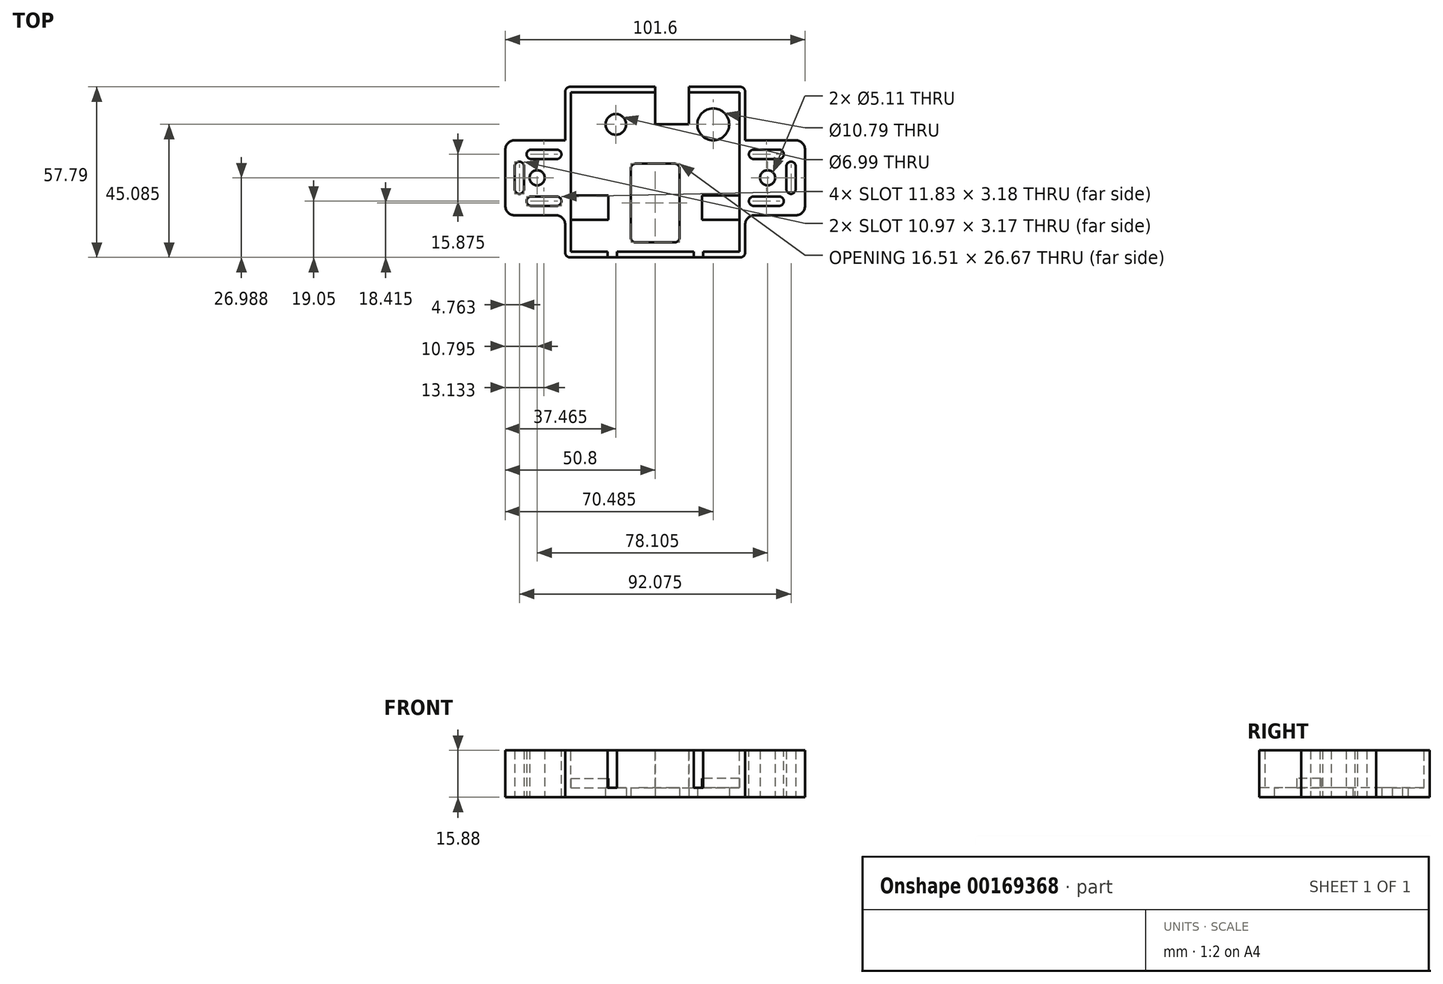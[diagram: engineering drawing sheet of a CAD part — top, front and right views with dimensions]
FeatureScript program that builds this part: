
annotation { "Feature Type Name" : "Feature", "Feature Type Description" : "" }
export const myFeature = defineFeature(function(context is Context, id is Id, definition is map)
    precondition{}
    {
        {
            var Q0;
            Q0=qCreatedBy(makeId("Top.planeOp"),FACE);
            var sketch = newSketch(context, id + "F0", { "sketchPlane" : qUnion([Q0])});
            skLineSegment(sketch, "E0.bottom", {"start": v(0, 0) * mm, "end": v(60.96, 0) * mm});
            skLineSegment(sketch, "E0.top", {"start": v(0, 57.78) * mm, "end": v(60.96, 57.78) * mm});
            skLineSegment(sketch, "E0.left", {"start": v(0, 0) * mm, "end": v(0, 57.78) * mm});
            skLineSegment(sketch, "E0.right", {"start": v(60.96, 0) * mm, "end": v(60.96, 57.79) * mm});
            skSolve(sketch);
        }
        {
            var Q0;
            Q0 = qSketchRegion(id + "F0", true);
            extrude(context, id + "F1", {"entities" : qUnion([Q0]), "depth" : 15.88 * mm});
        }
        {
            var Q0;
            Q0=makeQuery(id+"F1.opExtrude","CAP_FACE",FACE,{"disambiguationData":[OSD([sQuery(id+"F0.wireOp",EDGE,"E0.bottom"),sQuery(id+"F0.wireOp",EDGE,"E0.top"),sQuery(id+"F0.wireOp",EDGE,"E0.left"),sQuery(id+"F0.wireOp",EDGE,"E0.right")])],"isStart":false});
            var sketch = newSketch(context, id + "F2", { "sketchPlane" : qUnion([Q0])});
            skLineSegment(sketch, "E1.bottom", {"start": v(1.9, 55.88) * mm, "end": v(59.06, 55.88) * mm});
            skLineSegment(sketch, "E1.top", {"start": v(1.9, 1.9) * mm, "end": v(59.06, 1.9) * mm});
            skLineSegment(sketch, "E1.left", {"start": v(1.9, 55.88) * mm, "end": v(1.9, 1.9) * mm});
            skLineSegment(sketch, "E1.right", {"start": v(59.06, 55.88) * mm, "end": v(59.06, 1.9) * mm});
            skSolve(sketch);
        }
        {
            var Q0;
            Q0=makeQuery(id+"F2.imprint","IMPRINT",FACE,{"disambiguationData":[TD([[makeQuery(id+"F2.imprint","IMPRINT",EDGE,{"derivedFrom":sQuery(id+"F2.wireOp",EDGE,"E1.bottom")}),-1.0]])]});
            extrude(context, id + "F3", {"entities" : qUnion([Q0]), "operationType" : NewBodyOperationType.REMOVE, "oppositeDirection" : true, "depth" : 12.7 * mm});
        }
        {
            var Q0;
            Q0=makeQuery(id+"F1.opExtrude","CAP_FACE",FACE,{"disambiguationData":[OSD([sQuery(id+"F0.wireOp",EDGE,"E0.bottom"),sQuery(id+"F0.wireOp",EDGE,"E0.top"),sQuery(id+"F0.wireOp",EDGE,"E0.left"),sQuery(id+"F0.wireOp",EDGE,"E0.right")])],"isStart":true});
            var sketch = newSketch(context, id + "F4", { "sketchPlane" : qUnion([Q0])});
            skCircle(sketch, "E2", {"center": v(50.16, -45.08) * mm, "radius": 5.4 * mm});
            skLineSegment(sketch, "E3.bottom", {"start": v(41.91, -57.78) * mm, "end": v(30.48, -57.78) * mm});
            skLineSegment(sketch, "E3.top", {"start": v(41.91, -45.08) * mm, "end": v(30.48, -45.08) * mm});
            skLineSegment(sketch, "E3.left", {"start": v(41.91, -57.78) * mm, "end": v(41.91, -45.08) * mm});
            skLineSegment(sketch, "E3.right", {"start": v(30.48, -57.78) * mm, "end": v(30.48, -45.08) * mm});
            skCircle(sketch, "E4", {"center": v(17.15, -45.08) * mm, "radius": 3.5 * mm});
            skLineSegment(sketch, "E5.bottom", {"start": v(23.81, -5.08) * mm, "end": v(37.15, -5.08) * mm});
            skLineSegment(sketch, "E5.top", {"start": v(23.81, -31.75) * mm, "end": v(37.15, -31.75) * mm});
            skLineSegment(sketch, "E5.left", {"start": v(22.22, -6.67) * mm, "end": v(22.22, -30.16) * mm});
            skLineSegment(sketch, "E5.right", {"start": v(38.73, -6.67) * mm, "end": v(38.73, -30.16) * mm});
            skPoint(sketch, "E6", {"position": v(30.48, -5.08) * mm});
            skPoint(sketch, "E7", {"position": v(30.48, 0) * mm});
            skPoint(sketch, "E8.visualSharp", {"position": v(22.22, -5.08) * mm});
            skArc(sketch, "E8.filletArc", {"start": v(23.81, -5.08) * mm, "mid": v(22.69, -5.54) * mm, "end": v(22.22, -6.67) * mm});
            skPoint(sketch, "E9.visualSharp", {"position": v(38.74, -5.08) * mm});
            skArc(sketch, "E9.filletArc", {"start": v(38.74, -6.67) * mm, "mid": v(38.27, -5.54) * mm, "end": v(37.15, -5.08) * mm});
            skPoint(sketch, "E10.visualSharp", {"position": v(38.74, -31.75) * mm});
            skArc(sketch, "E10.filletArc", {"start": v(37.15, -31.75) * mm, "mid": v(38.27, -31.29) * mm, "end": v(38.74, -30.16) * mm});
            skPoint(sketch, "E11.visualSharp", {"position": v(22.22, -31.75) * mm});
            skArc(sketch, "E11.filletArc", {"start": v(22.22, -30.16) * mm, "mid": v(22.69, -31.29) * mm, "end": v(23.81, -31.75) * mm});
            skSolve(sketch);
        }
        {
            var Q0;
            Q0=makeQuery(id+"F4.imprint","IMPRINT",FACE,{"disambiguationData":[TD([[makeQuery(id+"F4.imprint","IMPRINT",EDGE,{"derivedFrom":sQuery(id+"F4.wireOp",EDGE,"E4")}),1.0]])]});
            var Q1;
            Q1=makeQuery(id+"F4.imprint","IMPRINT",FACE,{"disambiguationData":[TD([[makeQuery(id+"F4.imprint","IMPRINT",EDGE,{"derivedFrom":sQuery(id+"F4.wireOp",EDGE,"E2")}),1.0]])]});
            var Q2;
            Q2=makeQuery(id+"F4.imprint","IMPRINT",FACE,{"disambiguationData":[TD([[makeQuery(id+"F4.imprint","IMPRINT",EDGE,{"derivedFrom":sQuery(id+"F4.wireOp",EDGE,"E5.bottom")}),-1.0]])]});
            extrude(context, id + "F5", {"entities" : qUnion([Q0, Q1, Q2]), "operationType" : NewBodyOperationType.REMOVE, "endBound" : BoundingType.THROUGH_ALL, "oppositeDirection" : true, "depth" : 25.4 * mm});
        }
        {
            var Q0;
            Q0=makeQuery(id+"F3.boolean.opBoolean","COPY",FACE,{"derivedFrom":makeQuery(id+"F3.opExtrude","CAP_FACE",FACE,{"disambiguationData":[OSD([sQuery(id+"F2.wireOp",EDGE,"E1.bottom"),sQuery(id+"F2.wireOp",EDGE,"E1.top"),sQuery(id+"F2.wireOp",EDGE,"E1.left"),sQuery(id+"F2.wireOp",EDGE,"E1.right")])],"isStart":false})});
            var sketch = newSketch(context, id + "F6", { "sketchPlane" : qUnion([Q0])});
            skLineSegment(sketch, "E12.bottom", {"start": v(1.9, 12.7) * mm, "end": v(14.6, 12.7) * mm});
            skLineSegment(sketch, "E12.top", {"start": v(1.9, 20.95) * mm, "end": v(14.6, 20.95) * mm});
            skLineSegment(sketch, "E12.left", {"start": v(1.9, 12.7) * mm, "end": v(1.9, 20.95) * mm});
            skLineSegment(sketch, "E12.right", {"start": v(14.6, 12.7) * mm, "end": v(14.6, 20.95) * mm});
            skLineSegment(sketch, "E13.bottom", {"start": v(59.06, 12.7) * mm, "end": v(46.36, 12.7) * mm});
            skLineSegment(sketch, "E13.top", {"start": v(59.06, 20.96) * mm, "end": v(46.36, 20.96) * mm});
            skLineSegment(sketch, "E13.left", {"start": v(59.06, 12.7) * mm, "end": v(59.06, 20.96) * mm});
            skLineSegment(sketch, "E13.right", {"start": v(46.36, 12.7) * mm, "end": v(46.36, 20.96) * mm});
            skSolve(sketch);
        }
        {
            var Q0;
            Q0=makeQuery(id+"F6.imprint","IMPRINT",FACE,{"disambiguationData":[TD([[makeQuery(id+"F6.imprint","IMPRINT",EDGE,{"derivedFrom":sQuery(id+"F6.wireOp",EDGE,"E12.bottom")}),1.0]])]});
            var Q1;
            Q1=makeQuery(id+"F6.imprint","IMPRINT",FACE,{"disambiguationData":[TD([[makeQuery(id+"F6.imprint","IMPRINT",EDGE,{"derivedFrom":sQuery(id+"F6.wireOp",EDGE,"E13.bottom")}),-1.0]])]});
            extrude(context, id + "F7", {"entities" : qUnion([Q0, Q1]), "operationType" : NewBodyOperationType.ADD, "depth" : 3.17 * mm});
        }
        {
            var Q0;
            {var subQ3=sQuery(id+"F0.wireOp",EDGE,"E0.left");var subQ4=sQuery(id+"F0.wireOp",EDGE,"E0.top");Q0=makeQuery(id+"F13.boolean.opBoolean","SPLIT",FACE,{"disambiguationData":[TD([makeQuery(id+"F11.opFillet","BLEND_FACE",FACE,{"disambiguationData":[OSD([subQ4,subQ3])]})])],"derivedFrom":makeQuery(id+"F1.opExtrude","SWEPT_FACE",FACE,{"disambiguationData":[OSD([subQ3])]})});}
            var Q1;
            {var subQ0=sQuery(id+"F0.wireOp",EDGE,"E0.right");var subQ1=sQuery(id+"F0.wireOp",EDGE,"E0.top");Q1=makeQuery(id+"F13.boolean.opBoolean","SPLIT",FACE,{"disambiguationData":[TD([makeQuery(id+"F11.opFillet","BLEND_FACE",FACE,{"disambiguationData":[OSD([subQ1,subQ0])]})])],"derivedFrom":makeQuery(id+"F1.opExtrude","SWEPT_FACE",FACE,{"disambiguationData":[OSD([subQ0])]})});}
            cPlane(context, id + "F8", {"entities" : qUnion([Q0, Q1]), "cplaneType" : CPlaneType.MID_PLANE, "offset" : 25.4 * mm, "width" : 152.4 * mm, "height" : 152.4 * mm});
        }
        {
            var Q0;
            Q0=qCreatedBy(id+"F8.planeOp",FACE);
            var sketch = newSketch(context, id + "F9", { "sketchPlane" : qUnion([Q0])});
            skLineSegment(sketch, "E14", {"start": v(-57.22, -1.65) * mm, "end": v(-41.18, -1.65) * mm, "construction": true});
            skSolve(sketch);
        }
        {
            var Q0;
            Q0=makeQuery(id+"F4.imprint","IMPRINT",FACE,{"disambiguationData":[TD([[makeQuery(id+"F4.imprint","IMPRINT",EDGE,{"derivedFrom":sQuery(id+"F4.wireOp",EDGE,"E3.bottom")}),1.0]])]});
            extrude(context, id + "F10", {"entities" : qUnion([Q0]), "operationType" : NewBodyOperationType.REMOVE, "oppositeDirection" : true, "depth" : 25.4 * mm});
        }
        {
            var Q0;
            Q0=makeQuery(id+"F1.opExtrude","SWEPT_EDGE",EDGE,{"disambiguationData":[OSD([sQuery(id+"F0.wireOp",EDGE,"E0.top"),sQuery(id+"F0.wireOp",EDGE,"E0.left")])]});
            var Q1;
            Q1=makeQuery(id+"F1.opExtrude","SWEPT_EDGE",EDGE,{"disambiguationData":[OSD([sQuery(id+"F0.wireOp",EDGE,"E0.bottom"),sQuery(id+"F0.wireOp",EDGE,"E0.left")])]});
            var Q2;
            Q2=makeQuery(id+"F1.opExtrude","SWEPT_EDGE",EDGE,{"disambiguationData":[OSD([sQuery(id+"F0.wireOp",EDGE,"E0.top"),sQuery(id+"F0.wireOp",EDGE,"E0.right")])]});
            var Q3;
            Q3=makeQuery(id+"F1.opExtrude","SWEPT_EDGE",EDGE,{"disambiguationData":[OSD([sQuery(id+"F0.wireOp",EDGE,"E0.bottom"),sQuery(id+"F0.wireOp",EDGE,"E0.right")])]});
            fillet(context, id + "F11", {"entities" : qUnion([Q0, Q1, Q2, Q3]), "radius" : 1.59 * mm, "tangentPropagation" : true, "allowEdgeOverflow" : false});
        }
        {
            var Q0;
            Q0=qCreatedBy(makeId("Top.planeOp"),FACE);
            var sketch = newSketch(context, id + "F12", { "sketchPlane" : qUnion([Q0])});
            skLineSegment(sketch, "E15.bottom", {"start": v(-20.32, 39.69) * mm, "end": v(81.28, 39.69) * mm});
            skLineSegment(sketch, "E15.top", {"start": v(-20.32, 14.29) * mm, "end": v(81.28, 14.29) * mm});
            skLineSegment(sketch, "E15.left", {"start": v(-20.32, 39.69) * mm, "end": v(-20.32, 14.29) * mm});
            skLineSegment(sketch, "E15.right", {"start": v(81.28, 39.69) * mm, "end": v(81.28, 14.29) * mm});
            skPoint(sketch, "E16", {"position": v(30.48, 39.69) * mm});
            skPoint(sketch, "E17", {"position": v(-20.32, 26.99) * mm});
            skCircle(sketch, "E18", {"center": v(-9.53, 26.99) * mm, "radius": 2.55 * mm});
            skCircle(sketch, "E19", {"center": v(68.58, 26.99) * mm, "radius": 2.55 * mm});
            skLineSegment(sketch, "E20", {"start": v(0, 39.69) * mm, "end": v(0, 14.29) * mm});
            skLineSegment(sketch, "E21", {"start": v(60.96, 14.29) * mm, "end": v(60.96, 39.69) * mm});
            skLineSegment(sketch, "E22", {"start": v(62.23, 17.46) * mm, "end": v(78.1, 17.46) * mm});
            skLineSegment(sketch, "E23", {"start": v(78.1, 17.46) * mm, "end": v(78.1, 36.51) * mm});
            skLineSegment(sketch, "E24", {"start": v(78.1, 36.51) * mm, "end": v(62.23, 36.51) * mm});
            skLineSegment(sketch, "E25", {"start": v(62.23, 36.51) * mm, "end": v(62.23, 33.34) * mm});
            skLineSegment(sketch, "E26", {"start": v(62.23, 33.34) * mm, "end": v(74.93, 33.34) * mm});
            skLineSegment(sketch, "E27", {"start": v(74.93, 33.34) * mm, "end": v(74.93, 20.64) * mm});
            skLineSegment(sketch, "E28", {"start": v(74.93, 20.64) * mm, "end": v(62.23, 20.64) * mm});
            skLineSegment(sketch, "E29", {"start": v(62.23, 20.64) * mm, "end": v(62.23, 17.46) * mm});
            skPoint(sketch, "E30", {"position": v(74.93, 26.99) * mm});
            skLineSegment(sketch, "E31", {"start": v(78.1, 19.26) * mm, "end": v(74.93, 22.43) * mm});
            skLineSegment(sketch, "E32", {"start": v(73.13, 20.64) * mm, "end": v(76.3, 17.46) * mm});
            skLineSegment(sketch, "E33", {"start": v(73.13, 33.34) * mm, "end": v(76.3, 36.51) * mm});
            skLineSegment(sketch, "E34", {"start": v(74.93, 31.54) * mm, "end": v(78.1, 34.72) * mm});
            skLineSegment(sketch, "E35", {"start": v(78.1, 17.46) * mm, "end": v(74.93, 20.64) * mm, "construction": true});
            skLineSegment(sketch, "E36", {"start": v(74.93, 33.34) * mm, "end": v(78.1, 36.51) * mm, "construction": true});
            skLineSegment(sketch, "E37.MirrorCS", {"start": v(-1.27, 20.64) * mm, "end": v(-1.27, 17.46) * mm});
            skLineSegment(sketch, "E38.MirrorCS", {"start": v(-1.27, 17.46) * mm, "end": v(-17.15, 17.46) * mm});
            skLineSegment(sketch, "E39.MirrorCS", {"start": v(-13.97, 20.64) * mm, "end": v(-1.27, 20.64) * mm});
            skLineSegment(sketch, "E40.MirrorCS", {"start": v(-13.97, 33.34) * mm, "end": v(-13.97, 20.64) * mm});
            skLineSegment(sketch, "E41.MirrorCS", {"start": v(-1.27, 33.34) * mm, "end": v(-13.97, 33.34) * mm});
            skLineSegment(sketch, "E42.MirrorCS", {"start": v(-1.27, 36.51) * mm, "end": v(-1.27, 33.34) * mm});
            skLineSegment(sketch, "E43.MirrorCS", {"start": v(-17.15, 36.51) * mm, "end": v(-1.27, 36.51) * mm});
            skLineSegment(sketch, "E44.MirrorCS", {"start": v(-17.15, 17.46) * mm, "end": v(-17.15, 36.51) * mm});
            skLineSegment(sketch, "E45.MirrorCS", {"start": v(-12.17, 33.34) * mm, "end": v(-15.35, 36.51) * mm});
            skLineSegment(sketch, "E46.MirrorCS", {"start": v(-13.97, 31.54) * mm, "end": v(-17.15, 34.72) * mm});
            skLineSegment(sketch, "E47.MirrorCS", {"start": v(-12.17, 20.64) * mm, "end": v(-15.35, 17.46) * mm});
            skLineSegment(sketch, "E48.MirrorCS", {"start": v(-17.15, 19.26) * mm, "end": v(-13.97, 22.43) * mm});
            skSolve(sketch);
        }
        {
            var Q0;
            {var subQ0=sQuery(id+"F12.wireOp",EDGE,"E15.left");Q0=makeQuery(id+"F12.imprint","IMPRINT",FACE,{"disambiguationData":[TD([[makeQuery(id+"F12.imprint","IMPRINT",EDGE,{"derivedFrom":subQ0}),1.0]])]});}
            var Q1;
            {var subQ0=sQuery(id+"F12.wireOp",EDGE,"E15.right");Q1=makeQuery(id+"F12.imprint","IMPRINT",FACE,{"disambiguationData":[TD([[makeQuery(id+"F12.imprint","IMPRINT",EDGE,{"derivedFrom":subQ0}),-1.0]])]});}
            var Q2;
            {var subQ7=sQuery(id+"F12.wireOp",EDGE,"E31");Q2=makeQuery(id+"F12.imprint","IMPRINT",FACE,{"disambiguationData":[TD([[makeQuery(id+"F12.imprint","IMPRINT",EDGE,{"derivedFrom":subQ7}),1.0]])]});}
            var Q3;
            {var subQ3=sQuery(id+"F12.wireOp",EDGE,"E33");Q3=makeQuery(id+"F12.imprint","IMPRINT",FACE,{"disambiguationData":[TD([[makeQuery(id+"F12.imprint","IMPRINT",EDGE,{"derivedFrom":subQ3}),-1.0]])]});}
            var Q4;
            {var subQ4=sQuery(id+"F12.wireOp",EDGE,"E45.MirrorCS");Q4=makeQuery(id+"F12.imprint","IMPRINT",FACE,{"disambiguationData":[TD([[makeQuery(id+"F12.imprint","IMPRINT",EDGE,{"derivedFrom":subQ4}),1.0]])]});}
            var Q5;
            {var subQ7=sQuery(id+"F12.wireOp",EDGE,"E47.MirrorCS");Q5=makeQuery(id+"F12.imprint","IMPRINT",FACE,{"disambiguationData":[TD([[makeQuery(id+"F12.imprint","IMPRINT",EDGE,{"derivedFrom":subQ7}),-1.0]])]});}
            var Q6;
            Q6=makeQuery(id+"F1.opExtrude","CAP_FACE",FACE,{"disambiguationData":[OSD([sQuery(id+"F0.wireOp",EDGE,"E0.bottom"),sQuery(id+"F0.wireOp",EDGE,"E0.top"),sQuery(id+"F0.wireOp",EDGE,"E0.left"),sQuery(id+"F0.wireOp",EDGE,"E0.right")])],"isStart":false});
            extrude(context, id + "F13", {"entities" : qUnion([Q0, Q1, Q2, Q3, Q4, Q5]), "operationType" : NewBodyOperationType.ADD, "endBound" : BoundingType.UP_TO_SURFACE, "endBoundEntityFace" : qUnion([Q6]), "depth" : 25.4 * mm});
        }
        {
            var Q0;
            Q0=makeQuery(id+"F13.opExtrude","SWEPT_EDGE",EDGE,{"disambiguationData":[OSD([sQuery(id+"F12.wireOp",EDGE,"E15.top"),sQuery(id+"F12.wireOp",EDGE,"E15.left")])]});
            var Q1;
            Q1=makeQuery(id+"F13.opExtrude","SWEPT_EDGE",EDGE,{"disambiguationData":[OSD([sQuery(id+"F12.wireOp",EDGE,"E15.top"),sQuery(id+"F12.wireOp",EDGE,"E20")])]});
            var Q2;
            Q2=makeQuery(id+"F13.opExtrude","SWEPT_EDGE",EDGE,{"disambiguationData":[OSD([sQuery(id+"F12.wireOp",EDGE,"E15.bottom"),sQuery(id+"F12.wireOp",EDGE,"E15.left")])]});
            var Q3;
            Q3=makeQuery(id+"F13.opExtrude","SWEPT_EDGE",EDGE,{"disambiguationData":[OSD([sQuery(id+"F12.wireOp",EDGE,"E15.bottom"),sQuery(id+"F12.wireOp",EDGE,"E20")])]});
            var Q4;
            Q4=makeQuery(id+"F13.opExtrude","SWEPT_EDGE",EDGE,{"disambiguationData":[OSD([sQuery(id+"F12.wireOp",EDGE,"E15.top"),sQuery(id+"F12.wireOp",EDGE,"E21")])]});
            var Q5;
            Q5=makeQuery(id+"F13.opExtrude","SWEPT_EDGE",EDGE,{"disambiguationData":[OSD([sQuery(id+"F12.wireOp",EDGE,"E15.top"),sQuery(id+"F12.wireOp",EDGE,"E15.right")])]});
            var Q6;
            Q6=makeQuery(id+"F13.opExtrude","SWEPT_EDGE",EDGE,{"disambiguationData":[OSD([sQuery(id+"F12.wireOp",EDGE,"E15.bottom"),sQuery(id+"F12.wireOp",EDGE,"E15.right")])]});
            var Q7;
            Q7=makeQuery(id+"F13.opExtrude","SWEPT_EDGE",EDGE,{"disambiguationData":[OSD([sQuery(id+"F12.wireOp",EDGE,"E15.bottom"),sQuery(id+"F12.wireOp",EDGE,"E21")])]});
            fillet(context, id + "F14", {"entities" : qUnion([Q0, Q1, Q2, Q3, Q4, Q5, Q6, Q7]), "radius" : 3.17 * mm, "tangentPropagation" : true, "allowEdgeOverflow" : false});
        }
        {
            var Q0;
            Q0=makeQuery(id+"F13.opExtrude","SWEPT_EDGE",EDGE,{"disambiguationData":[OSD([sQuery(id+"F12.wireOp",EDGE,"E22"),sQuery(id+"F12.wireOp",EDGE,"E29")])]});
            var Q1;
            Q1=makeQuery(id+"F13.opExtrude","SWEPT_EDGE",EDGE,{"disambiguationData":[OSD([sQuery(id+"F12.wireOp",EDGE,"E28"),sQuery(id+"F12.wireOp",EDGE,"E29")])]});
            var Q2;
            Q2=makeQuery(id+"F13.opExtrude","SWEPT_EDGE",EDGE,{"disambiguationData":[OSD([sQuery(id+"F12.wireOp",EDGE,"E25"),sQuery(id+"F12.wireOp",EDGE,"E26")])]});
            var Q3;
            Q3=makeQuery(id+"F13.opExtrude","SWEPT_EDGE",EDGE,{"disambiguationData":[OSD([sQuery(id+"F12.wireOp",EDGE,"E24"),sQuery(id+"F12.wireOp",EDGE,"E25")])]});
            var Q4;
            Q4=makeQuery(id+"F13.opExtrude","SWEPT_EDGE",EDGE,{"disambiguationData":[OSD([sQuery(id+"F12.wireOp",EDGE,"E22"),sQuery(id+"F12.wireOp",EDGE,"E23")])]});
            var Q5;
            Q5=makeQuery(id+"F13.opExtrude","SWEPT_EDGE",EDGE,{"disambiguationData":[OSD([sQuery(id+"F12.wireOp",EDGE,"E27"),sQuery(id+"F12.wireOp",EDGE,"E28")])]});
            var Q6;
            Q6=makeQuery(id+"F13.opExtrude","SWEPT_EDGE",EDGE,{"disambiguationData":[OSD([sQuery(id+"F12.wireOp",EDGE,"E26"),sQuery(id+"F12.wireOp",EDGE,"E27")])]});
            var Q7;
            Q7=makeQuery(id+"F13.opExtrude","SWEPT_EDGE",EDGE,{"disambiguationData":[OSD([sQuery(id+"F12.wireOp",EDGE,"E23"),sQuery(id+"F12.wireOp",EDGE,"E24")])]});
            var Q8;
            Q8=makeQuery(id+"F13.opExtrude","SWEPT_EDGE",EDGE,{"disambiguationData":[OSD([sQuery(id+"F12.wireOp",EDGE,"E41.MirrorCS"),sQuery(id+"F12.wireOp",EDGE,"E42.MirrorCS")])]});
            var Q9;
            Q9=makeQuery(id+"F13.opExtrude","SWEPT_EDGE",EDGE,{"disambiguationData":[OSD([sQuery(id+"F12.wireOp",EDGE,"E42.MirrorCS"),sQuery(id+"F12.wireOp",EDGE,"E43.MirrorCS")])]});
            var Q10;
            Q10=makeQuery(id+"F13.opExtrude","SWEPT_EDGE",EDGE,{"disambiguationData":[OSD([sQuery(id+"F12.wireOp",EDGE,"E43.MirrorCS"),sQuery(id+"F12.wireOp",EDGE,"E45.MirrorCS")])]});
            var Q11;
            Q11=makeQuery(id+"F13.opExtrude","SWEPT_EDGE",EDGE,{"disambiguationData":[OSD([sQuery(id+"F12.wireOp",EDGE,"E41.MirrorCS"),sQuery(id+"F12.wireOp",EDGE,"E45.MirrorCS")])]});
            var Q12;
            Q12=makeQuery(id+"F13.opExtrude","SWEPT_EDGE",EDGE,{"disambiguationData":[OSD([sQuery(id+"F12.wireOp",EDGE,"E38.MirrorCS"),sQuery(id+"F12.wireOp",EDGE,"E47.MirrorCS")])]});
            var Q13;
            Q13=makeQuery(id+"F13.opExtrude","SWEPT_EDGE",EDGE,{"disambiguationData":[OSD([sQuery(id+"F12.wireOp",EDGE,"E39.MirrorCS"),sQuery(id+"F12.wireOp",EDGE,"E47.MirrorCS")])]});
            var Q14;
            Q14=makeQuery(id+"F13.opExtrude","SWEPT_EDGE",EDGE,{"disambiguationData":[OSD([sQuery(id+"F12.wireOp",EDGE,"E37.MirrorCS"),sQuery(id+"F12.wireOp",EDGE,"E38.MirrorCS")])]});
            var Q15;
            Q15=makeQuery(id+"F13.opExtrude","SWEPT_EDGE",EDGE,{"disambiguationData":[OSD([sQuery(id+"F12.wireOp",EDGE,"E37.MirrorCS"),sQuery(id+"F12.wireOp",EDGE,"E39.MirrorCS")])]});
            var Q16;
            Q16=makeQuery(id+"F13.opExtrude","SWEPT_EDGE",EDGE,{"disambiguationData":[OSD([sQuery(id+"F12.wireOp",EDGE,"E44.MirrorCS"),sQuery(id+"F12.wireOp",EDGE,"E48.MirrorCS")])]});
            var Q17;
            Q17=makeQuery(id+"F13.opExtrude","SWEPT_EDGE",EDGE,{"disambiguationData":[OSD([sQuery(id+"F12.wireOp",EDGE,"E40.MirrorCS"),sQuery(id+"F12.wireOp",EDGE,"E48.MirrorCS")])]});
            var Q18;
            Q18=makeQuery(id+"F13.opExtrude","SWEPT_EDGE",EDGE,{"disambiguationData":[OSD([sQuery(id+"F12.wireOp",EDGE,"E44.MirrorCS"),sQuery(id+"F12.wireOp",EDGE,"E46.MirrorCS")])]});
            var Q19;
            Q19=makeQuery(id+"F13.opExtrude","SWEPT_EDGE",EDGE,{"disambiguationData":[OSD([sQuery(id+"F12.wireOp",EDGE,"E40.MirrorCS"),sQuery(id+"F12.wireOp",EDGE,"E46.MirrorCS")])]});
            fillet(context, id + "F15", {"entities" : qUnion([Q0, Q1, Q2, Q3, Q4, Q5, Q6, Q7, Q8, Q9, Q10, Q11, Q12, Q13, Q14, Q15, Q16, Q17, Q18, Q19]), "radius" : 1.59 * mm, "tangentPropagation" : true, "allowEdgeOverflow" : false});
        }
        {
            var Q0;
            Q0=makeQuery(id+"F1.opExtrude","SWEPT_FACE",FACE,{"disambiguationData":[OSD([sQuery(id+"F0.wireOp",EDGE,"E0.bottom")])]});
            var sketch = newSketch(context, id + "F16", { "sketchPlane" : qUnion([Q0])});
            skLineSegment(sketch, "E49.bottom", {"start": v(14.29, 3.18) * mm, "end": v(17.46, 3.18) * mm});
            skLineSegment(sketch, "E49.top", {"start": v(14.29, 15.88) * mm, "end": v(17.46, 15.88) * mm});
            skLineSegment(sketch, "E49.left", {"start": v(14.29, 3.18) * mm, "end": v(14.29, 15.88) * mm});
            skLineSegment(sketch, "E49.right", {"start": v(17.46, 3.18) * mm, "end": v(17.46, 15.88) * mm});
            skLineSegment(sketch, "E50.top", {"start": v(43.5, 15.88) * mm, "end": v(46.67, 15.88) * mm});
            skLineSegment(sketch, "E50.left", {"start": v(43.5, 3.18) * mm, "end": v(43.5, 15.88) * mm});
            skLineSegment(sketch, "E50.right", {"start": v(46.67, 3.18) * mm, "end": v(46.67, 15.88) * mm});
            skLineSegment(sketch, "E51", {"start": v(43.5, 3.18) * mm, "end": v(46.67, 3.18) * mm});
            skSolve(sketch);
        }
        {
            var Q0;
            Q0=makeQuery(id+"F16.imprint","IMPRINT",FACE,{"disambiguationData":[TD([[makeQuery(id+"F16.imprint","IMPRINT",EDGE,{"derivedFrom":sQuery(id+"F16.wireOp",EDGE,"E49.bottom")}),1.0]])]});
            var Q1;
            Q1=makeQuery(id+"F16.imprint","IMPRINT",FACE,{"disambiguationData":[TD([[makeQuery(id+"F16.imprint","IMPRINT",EDGE,{"derivedFrom":sQuery(id+"F16.wireOp",EDGE,"E50.bottom")}),1.0]])]});
            var Q2;
            Q2=makeQuery(id+"F16.imprint","IMPRINT",FACE,{"disambiguationData":[TD([[makeQuery(id+"F16.imprint","IMPRINT",EDGE,{"derivedFrom":sQuery(id+"F16.wireOp",EDGE,"E50.top")}),-1.0]])]});
            var Q3;
            Q3=makeQuery(id+"F3.boolean.opBoolean","COPY",FACE,{"derivedFrom":makeQuery(id+"F3.opExtrude","SWEPT_FACE",FACE,{"disambiguationData":[OSD([sQuery(id+"F2.wireOp",EDGE,"E1.top")])]})});
            extrude(context, id + "F17", {"entities" : qUnion([Q0, Q1, Q2]), "operationType" : NewBodyOperationType.REMOVE, "endBound" : BoundingType.UP_TO_SURFACE, "oppositeDirection" : true, "endBoundEntityFace" : qUnion([Q3]), "depth" : 25.4 * mm});
        }
    });
